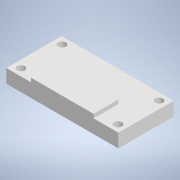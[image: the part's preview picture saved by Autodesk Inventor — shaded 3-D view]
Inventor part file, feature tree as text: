
AUTODESK INVENTOR PART (.ipt)
format: ipt  version: 2022 (Build 260153000, 153)  size: 124,416 bytes
history: native  units: mm
features: extrude x3, sketch x3, other x1, projected_geometry x1
ambient origin geometry x8: Origin, YZ Plane, XZ Plane, XY Plane, X Axis, Y Axis, Z Axis, Center Point
bodies: Body1 (feature_tree)
feature tree (8):
  other  "Твердое тело1"
  extrude  "Выдавливание1"  Depth=30.0mm
  extrude  "Выдавливание2"  Depth=14.8mm
  extrude  "Выдавливание3"  Depth=3.65mm TaperAngle=0.0deg
  sketch  "Эскиз1"
  sketch  "Эскиз2"
  sketch  "Эскиз3"
  projected_geometry  "Спроецированная петля1"
